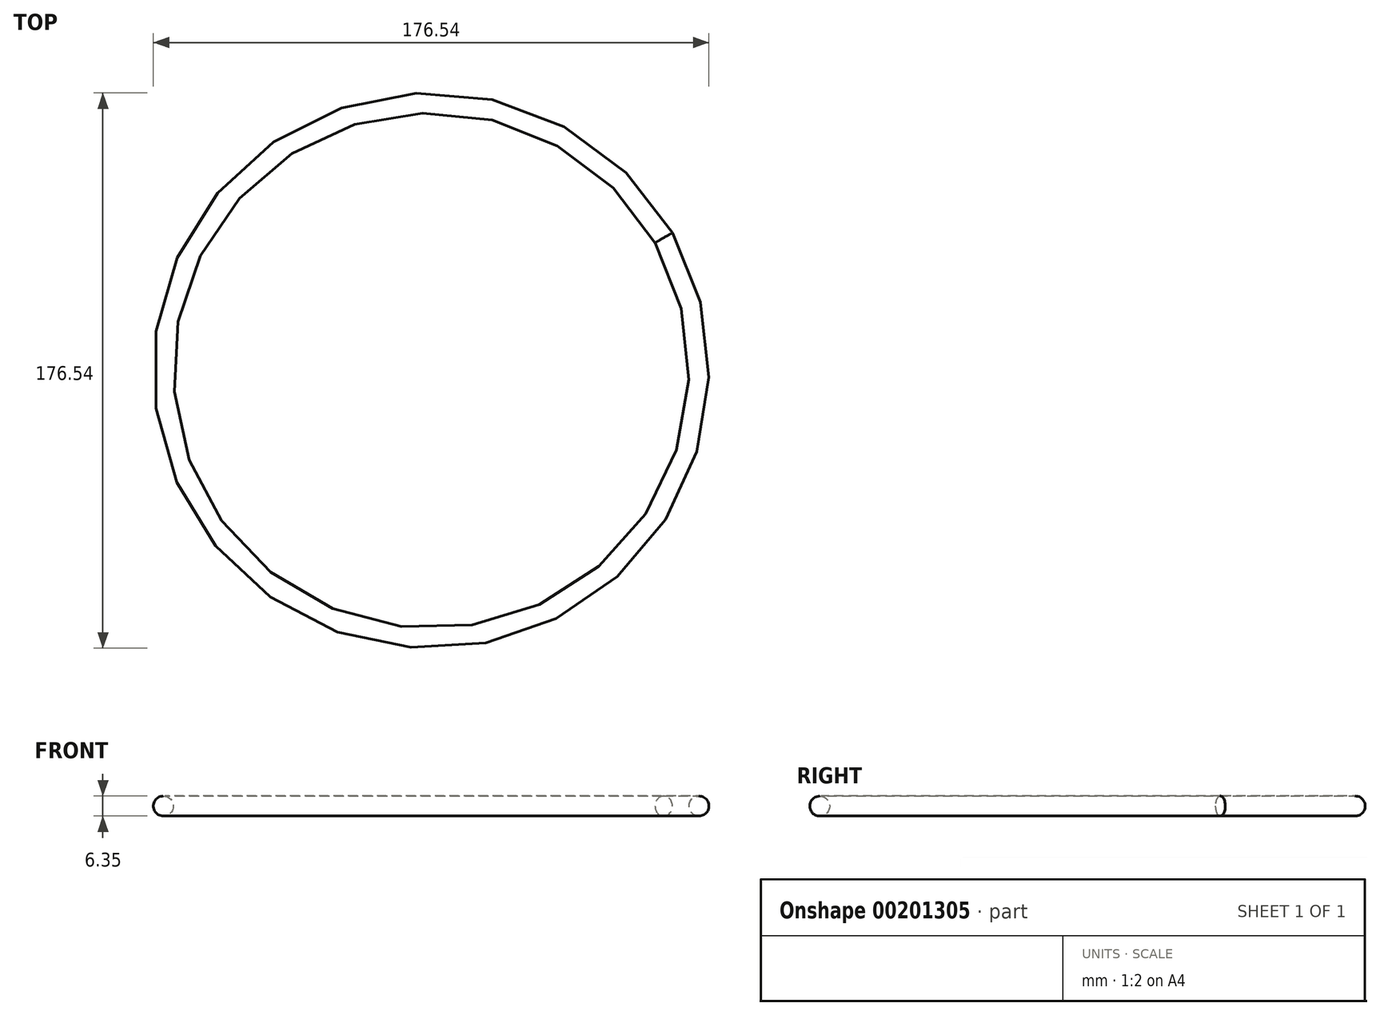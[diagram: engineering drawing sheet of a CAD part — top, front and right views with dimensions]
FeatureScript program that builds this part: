
annotation { "Feature Type Name" : "Feature", "Feature Type Description" : "" }
export const myFeature = defineFeature(function(context is Context, id is Id, definition is map)
    precondition{}
    {
        {
            var Q0;
            Q0=qCreatedBy(makeId("Top.planeOp"),FACE);
            var sketch = newSketch(context, id + "F0", { "sketchPlane" : qUnion([Q0])});
            skCircle(sketch, "E0", {"center": v(0, 0) * mm, "radius": 88.27 * mm});
            skLineSegment(sketch, "E1", {"start": v(-48, 74.08) * mm, "end": v(-44.54, 68.75) * mm});
            skCircle(sketch, "E2", {"center": v(0, 0) * mm, "radius": 81.92 * mm});
            skLineSegment(sketch, "E3", {"start": v(0, 0) * mm, "end": v(76.71, 43.65) * mm});
            skCircle(sketch, "E4", {"center": v(0, 0) * mm, "radius": 8.39 * mm});
            skLineSegment(sketch, "E5", {"start": v(0, 0) * mm, "end": v(76.64, 43.79) * mm});
            skSolve(sketch);
        }
        {
            var Q0;
            {var subQ0=sQuery(id+"F0.wireOp",EDGE,"E3");var subQ1=sQuery(id+"F0.wireOp",EDGE,"E0");var subQ2=makeQuery(id+"F0.imprint","INTERSECT",VERTEX,{"derivedFrom":[subQ1,subQ0]});Q0=makeQuery(id+"F0.imprint","IMPRINT",FACE,{"disambiguationData":[TD([[makeQuery(id+"F0.imprint","IMPRINT",EDGE,{"disambiguationData":[TD([[subQ2,-1.0]])],"derivedFrom":subQ1}),1.0]])]});}
            extrude(context, id + "F1", {"entities" : qUnion([Q0]), "depth" : 6.35 * mm});
        }
        {
            var Q0;
            Q0=makeQuery(id+"F1.opExtrude","SWEPT_FACE",FACE,{"disambiguationData":[OSD([sQuery(id+"F0.wireOp",EDGE,"E3")])]});
            var sketch = newSketch(context, id + "F2", { "sketchPlane" : qUnion([Q0])});
            skLineSegment(sketch, "E6", {"start": v(85.1, 0) * mm, "end": v(85.1, 6.35) * mm});
            skCircle(sketch, "E7", {"center": v(85.1, 3.18) * mm, "radius": 3.17 * mm});
            skLineSegment(sketch, "E8", {"start": v(0, 0) * mm, "end": v(0, 32.12) * mm});
            skSolve(sketch);
        }
        {
            var Q0;
            {var subQ0=sQuery(id+"F2.wireOp",EDGE,"E7");var subQ1=sQuery(id+"F0.wireOp",EDGE,"E3");var subQ2=makeQuery(id+"F1.opExtrude","CAP_EDGE",EDGE,{"disambiguationData":[OSD([subQ1])],"isStart":false});var subQ3=makeQuery(id+"F2.imprint","INTERSECT",VERTEX,{"derivedFrom":[subQ2,sQuery(id+"F2.wireOp",EDGE,"E6"),subQ0]});Q0=makeQuery(id+"F2.imprint","IMPRINT",FACE,{"disambiguationData":[TD([[makeQuery(id+"F2.imprint","IMPRINT",EDGE,{"disambiguationData":[TD([[subQ3,-1.0]])],"derivedFrom":subQ0}),-1.0]])]});}
            var Q1;
            {var subQ0=sQuery(id+"F2.wireOp",EDGE,"E7");var subQ1=sQuery(id+"F0.wireOp",EDGE,"E3");var subQ2=makeQuery(id+"F1.opExtrude","CAP_EDGE",EDGE,{"disambiguationData":[OSD([subQ1])],"isStart":false});var subQ3=makeQuery(id+"F2.imprint","INTERSECT",VERTEX,{"derivedFrom":[subQ2,sQuery(id+"F2.wireOp",EDGE,"E6"),subQ0]});Q1=makeQuery(id+"F2.imprint","IMPRINT",FACE,{"disambiguationData":[TD([[makeQuery(id+"F2.imprint","IMPRINT",EDGE,{"disambiguationData":[TD([[subQ3,1.0]])],"derivedFrom":subQ0}),-1.0]])]});}
            var Q2;
            {var subQ0=sQuery(id+"F2.wireOp",EDGE,"E7");var subQ1=sQuery(id+"F0.wireOp",EDGE,"E3");var subQ2=makeQuery(id+"F1.opExtrude","CAP_EDGE",EDGE,{"disambiguationData":[OSD([subQ1])],"isStart":true});var subQ3=makeQuery(id+"F2.imprint","INTERSECT",VERTEX,{"derivedFrom":[subQ2,sQuery(id+"F2.wireOp",EDGE,"E6"),subQ0]});Q2=makeQuery(id+"F2.imprint","IMPRINT",FACE,{"disambiguationData":[TD([[makeQuery(id+"F2.imprint","IMPRINT",EDGE,{"disambiguationData":[TD([[subQ3,-1.0]])],"derivedFrom":subQ0}),-1.0]])]});}
            var Q3;
            {var subQ0=sQuery(id+"F2.wireOp",EDGE,"E7");var subQ1=sQuery(id+"F0.wireOp",EDGE,"E3");var subQ2=makeQuery(id+"F1.opExtrude","CAP_EDGE",EDGE,{"disambiguationData":[OSD([subQ1])],"isStart":true});var subQ3=makeQuery(id+"F2.imprint","INTERSECT",VERTEX,{"derivedFrom":[subQ2,sQuery(id+"F2.wireOp",EDGE,"E6"),subQ0]});Q3=makeQuery(id+"F2.imprint","IMPRINT",FACE,{"disambiguationData":[TD([[makeQuery(id+"F2.imprint","IMPRINT",EDGE,{"disambiguationData":[TD([[subQ3,1.0]])],"derivedFrom":subQ0}),-1.0]])]});}
            extrude(context, id + "F3", {"entities" : qUnion([Q0, Q1, Q2, Q3]), "operationType" : NewBodyOperationType.REMOVE, "endBound" : BoundingType.THROUGH_ALL, "oppositeDirection" : true, "depth" : 25.4 * mm});
        }
        {
            var Q0;
            {var subQ0=sQuery(id+"F2.wireOp",EDGE,"E6");Q0=makeQuery(id+"F2.imprint","IMPRINT",FACE,{"disambiguationData":[TD([[makeQuery(id+"F2.imprint","IMPRINT",EDGE,{"derivedFrom":subQ0}),-1.0]])]});}
            var Q1;
            {var subQ0=sQuery(id+"F2.wireOp",EDGE,"E6");Q1=makeQuery(id+"F2.imprint","IMPRINT",FACE,{"disambiguationData":[TD([[makeQuery(id+"F2.imprint","IMPRINT",EDGE,{"derivedFrom":subQ0}),1.0]])]});}
            var Q2;
            Q2=sQuery(id+"F2.wireOp",EDGE,"E8");
            revolve(context, id + "F4", {"operationType" : NewBodyOperationType.ADD, "entities" : qUnion([Q0, Q1]), "axis" : qUnion([Q2]), "revolveType" : RevolveType.FULL});
        }
    });
